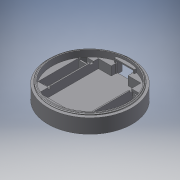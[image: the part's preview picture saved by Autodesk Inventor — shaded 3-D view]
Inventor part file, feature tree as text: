
AUTODESK INVENTOR PART (.ipt)
format: ipt  version: 2016 SP2 (Build 200236200, 236)  size: 533,504 bytes
history: native  units: mm
features: sketch x13, extrude x9, revolve x3, thread x2, other x1
ambient origin geometry x8: Origin, YZ Plane, XZ Plane, XY Plane, X Axis, Y Axis, Z Axis, Center Point
bodies: Volumenkörper1 (feature_tree), Volumenkörper3 (feature_tree)
feature tree (28):
  revolve  "Umdrehung1"
  thread  "Gewinde1"  [1 undecoded]
  extrude  "Extrusion1"  Depth=20.0mm
  extrude  "Extrusion2"  Depth=2.3mm
  extrude  "Extrusion3"  TaperAngle=90.0deg  [1 undecoded]
  thread  "Gewinde2"  [1 undecoded]
  revolve  "Umdrehung4"
  revolve  "Umdrehung5"
  other  "Spirale2"
  extrude  "Extrusion4"  Depth=35.35mm
  extrude  "Extrusion5"  Depth=8.4mm
  extrude  "Extrusion6"  Depth=10.5mm TaperAngle=0.0deg
  extrude  "Extrusion7"  Depth=3.0mm
  extrude  "Extrusion8"  Depth=3.0mm
  extrude  "Extrusion9"  Depth=3.8mm TaperAngle=0.0deg
  sketch  "Skizze1"  dims[d1=20.0mm d2=5.0mm]
  sketch  "Skizze5"  dims[d3=2.0mm d4=2.3mm]
  sketch  "Skizze6"  dims[d5=3.0mm d6=90.0deg d7=10.0mm d8=0.0mm]
  sketch  "Skizze7"  dims[d16=60.0deg]
  sketch  "Skizze8"  dims[d28=50.7mm d29=70.7mm d32=11.0mm d33=11.0mm d34=48.3mm d35=48.3mm d36=1.2mm d37=1.2mm d38=0.8mm d39=0.8mm d40=0.8mm d41=3.0mm d42=3.75mm d43=2.0mm d44=3.0mm d45=0.5mm d46=0.5mm d47=0.8mm d48=0.5mm d49=3.0mm d50=3.75mm d51=2.0mm d52=0.5mm d53=3.0mm d54=0.8mm d55=0.8mm d56=1.6mm d57=1.0mm d58=1.0mm d59=1.0mm d60=1.0mm d61=1.0mm d62=1.0mm d63=1.6mm d64=0.5mm d65=35.35mm]
  sketch  "Skizze9"  dims[d66=25.35mm d67=8.4mm]
  sketch  "Skizze10"  dims[d68=11.0mm d69=10.5mm d70=0.0mm]
  sketch  "Skizze11"  dims[d71=3.0mm d72=3.0mm]
  sketch  "Skizze12"  dims[d73=3.8mm d74=0.0mm d75=3.0mm]
  sketch  "Skizze13"  dims[d76=3.0mm d77=3.8mm d78=0.0mm]
  sketch  "Skizze14"  dims[d79=10.0mm d80=0.0mm]
  sketch  "Skizze15"  dims[d81=60.0deg d82=0.320166mm d83=0.320166mm]
  sketch  "Skizze16"  dims[d86=2.0mm d88=60.0deg d90=0.0mm d91=0.0mm d92=2.002mm d93=7.0mm d94=10.0mm d95=0.0mm d96=0.0mm d97=0.0mm d98=0.0mm d99=0.0mm d100=19.0mm d101=11.5mm d102=7.0mm d103=0.0mm d104=21.0mm d105=15.5mm d106=9.5mm d107=0.0mm d108=4.0mm d109=4.0mm d110=5.75mm d111=5.75mm d112=3.0mm d113=3.0mm d114=4.0mm d115=4.0mm d116=2.0mm d117=0.0mm d118=20.0mm d119=5.0mm d120=0.0mm d121=1.5mm d122=9.75mm d123=0.0mm d124=5.5mm d125=0.0mm]
note: 3 required parameter values undecoded (feature->parameter linkage not recoverable at this tier; creation-order binding heuristic only, values carry confidence <= 0.55)
